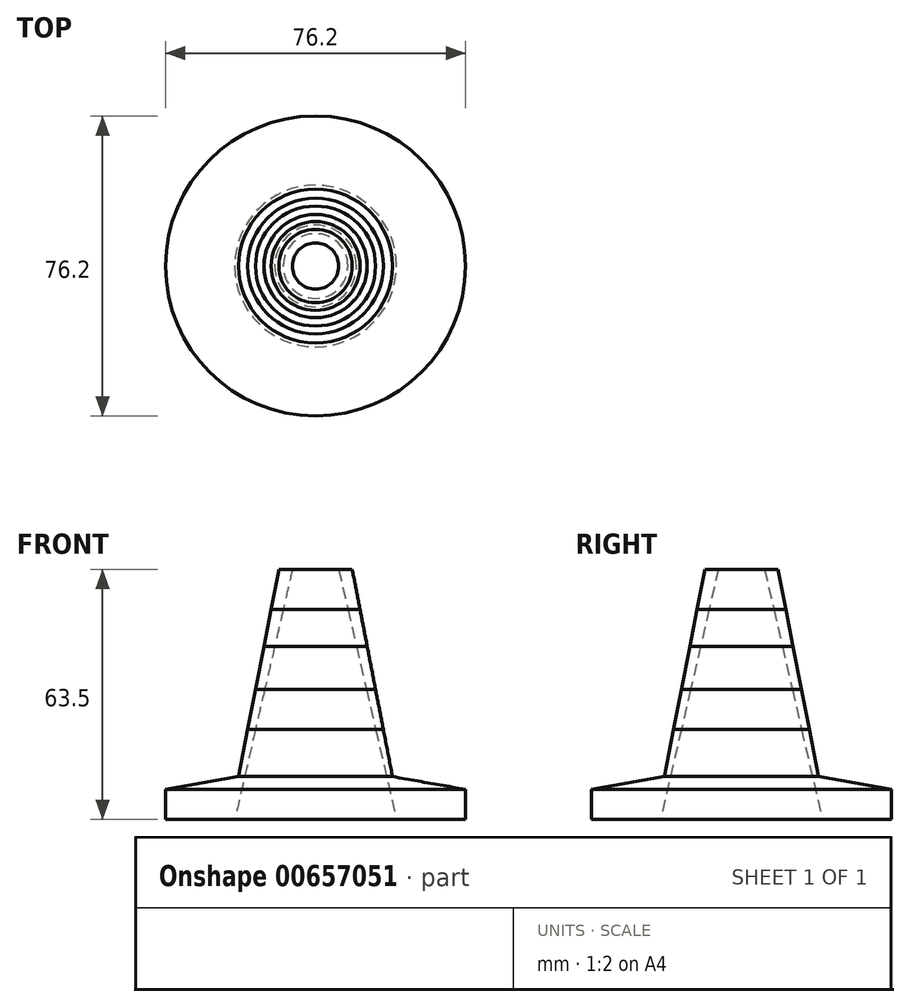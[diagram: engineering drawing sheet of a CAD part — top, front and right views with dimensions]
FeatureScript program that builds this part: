
annotation { "Feature Type Name" : "Feature", "Feature Type Description" : "" }
export const myFeature = defineFeature(function(context is Context, id is Id, definition is map)
    precondition{}
    {
        {
            var Q0;
            Q0=qCreatedBy(makeId("Front.planeOp"),FACE);
            var sketch = newSketch(context, id + "F0", { "sketchPlane" : qUnion([Q0])});
            skLineSegment(sketch, "E0", {"start": v(-38.1, 0) * mm, "end": v(-38.1, 7.62) * mm});
            skLineSegment(sketch, "E1", {"start": v(-38.1, 7.62) * mm, "end": v(-19.55, 10.9) * mm});
            skLineSegment(sketch, "E2", {"start": v(-19.55, 10.9) * mm, "end": v(-9.32, 63.5) * mm});
            skLineSegment(sketch, "E3", {"start": v(-9.32, 63.5) * mm, "end": v(0, 63.5) * mm});
            skLineSegment(sketch, "E4", {"start": v(0, 63.5) * mm, "end": v(0, 0) * mm});
            skLineSegment(sketch, "E5", {"start": v(0, 0) * mm, "end": v(-38.1, 0) * mm});
            skLineSegment(sketch, "E6", {"start": v(-17.22, 22.86) * mm, "end": v(0, 22.86) * mm});
            skLineSegment(sketch, "E7", {"start": v(-15.25, 33.02) * mm, "end": v(0, 33.02) * mm});
            skLineSegment(sketch, "E8", {"start": v(-13.13, 43.94) * mm, "end": v(0, 43.94) * mm});
            skLineSegment(sketch, "E9", {"start": v(-11.3, 53.34) * mm, "end": v(0, 53.34) * mm});
            skSolve(sketch);
        }
        {
            var Q0;
            {var subQ0=sQuery(id+"F0.wireOp",EDGE,"E3");Q0=makeQuery(id+"F0.imprint","IMPRINT",FACE,{"disambiguationData":[TD([[makeQuery(id+"F0.imprint","IMPRINT",EDGE,{"derivedFrom":subQ0}),-1.0]])]});}
            var Q1;
            Q1=sQuery(id+"F0.wireOp",EDGE,"E4");
            revolve(context, id + "F1", {"entities" : qUnion([Q0]), "axis" : qUnion([Q1]), "revolveType" : RevolveType.FULL});
        }
        {
            var Q0;
            {var subQ0=sQuery(id+"F0.wireOp",EDGE,"E8");Q0=makeQuery(id+"F0.imprint","IMPRINT",FACE,{"disambiguationData":[TD([[makeQuery(id+"F0.imprint","IMPRINT",EDGE,{"derivedFrom":subQ0}),1.0]])]});}
            var Q1;
            Q1=sQuery(id+"F0.wireOp",EDGE,"E4");
            revolve(context, id + "F2", {"entities" : qUnion([Q0]), "axis" : qUnion([Q1]), "revolveType" : RevolveType.FULL});
        }
        {
            var Q0;
            {var subQ0=sQuery(id+"F0.wireOp",EDGE,"E7");Q0=makeQuery(id+"F0.imprint","IMPRINT",FACE,{"disambiguationData":[TD([[makeQuery(id+"F0.imprint","IMPRINT",EDGE,{"derivedFrom":subQ0}),1.0]])]});}
            var Q1;
            Q1=sQuery(id+"F0.wireOp",EDGE,"E4");
            revolve(context, id + "F3", {"entities" : qUnion([Q0]), "axis" : qUnion([Q1]), "revolveType" : RevolveType.FULL});
        }
        {
            var Q0;
            {var subQ0=sQuery(id+"F0.wireOp",EDGE,"E6");Q0=makeQuery(id+"F0.imprint","IMPRINT",FACE,{"disambiguationData":[TD([[makeQuery(id+"F0.imprint","IMPRINT",EDGE,{"derivedFrom":subQ0}),1.0]])]});}
            var Q1;
            Q1=sQuery(id+"F0.wireOp",EDGE,"E4");
            revolve(context, id + "F4", {"entities" : qUnion([Q0]), "axis" : qUnion([Q1]), "revolveType" : RevolveType.FULL});
        }
        {
            var Q0;
            Q0=makeQuery(id+"F0.imprint","IMPRINT",FACE,{"disambiguationData":[TD([[makeQuery(id+"F0.imprint","IMPRINT",EDGE,{"derivedFrom":sQuery(id+"F0.wireOp",EDGE,"E0")}),-1.0]])]});
            var Q1;
            Q1=sQuery(id+"F0.wireOp",EDGE,"E4");
            revolve(context, id + "F5", {"entities" : qUnion([Q0]), "axis" : qUnion([Q1]), "revolveType" : RevolveType.FULL});
        }
        {
            var Q0;
            Q0=makeQuery(id+"F5.opRevolve","SWEPT_FACE",FACE,{"disambiguationData":[OSD([sQuery(id+"F0.wireOp",EDGE,"E5")])]});
            var sketch = newSketch(context, id + "F6", { "sketchPlane" : qUnion([Q0])});
            skCircle(sketch, "E10", {"center": v(0, 0) * mm, "radius": 20.54 * mm});
            skSolve(sketch);
        }
        {
            var Q0;
            Q0 = qSketchRegion(id + "F6", true);
            extrude(context, id + "F7", {"entities" : qUnion([Q0]), "operationType" : NewBodyOperationType.REMOVE, "endBound" : BoundingType.THROUGH_ALL, "oppositeDirection" : true, "depth" : 25.4 * mm, "offsetDistance" : 25.4 * mm, "hasDraft" : true, "draftAngle" : 13 * degree, "draftPullDirection" : true});
        }
    });
